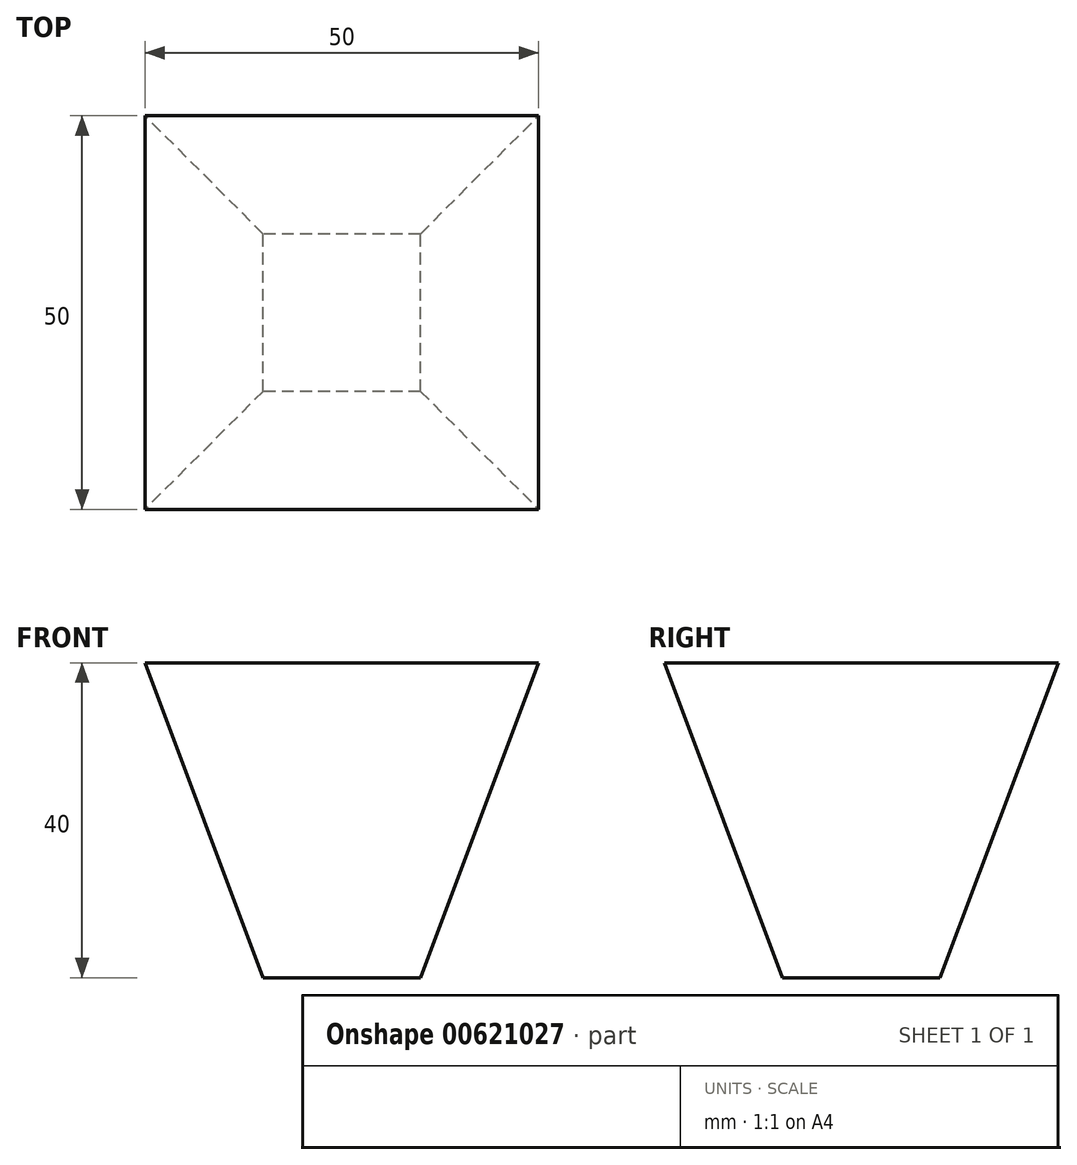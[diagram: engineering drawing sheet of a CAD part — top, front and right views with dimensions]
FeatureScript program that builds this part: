
annotation { "Feature Type Name" : "Feature", "Feature Type Description" : "" }
export const myFeature = defineFeature(function(context is Context, id is Id, definition is map)
    precondition{}
    {
        {
            var Q0;
            Q0=qCreatedBy(makeId("Top.planeOp"),FACE);
            var sketch = newSketch(context, id + "F0", { "sketchPlane" : qUnion([Q0])});
            skLineSegment(sketch, "E0.bottom", {"start": v(10, -10) * mm, "end": v(-10, -10) * mm});
            skLineSegment(sketch, "E0.top", {"start": v(10, 10) * mm, "end": v(-10, 10) * mm});
            skLineSegment(sketch, "E0.left", {"start": v(10, -10) * mm, "end": v(10, 10) * mm});
            skLineSegment(sketch, "E0.right", {"start": v(-10, -10) * mm, "end": v(-10, 10) * mm});
            skPoint(sketch, "E0.middle", {"position": v(0, 0) * mm});
            skSolve(sketch);
        }
        {
            var Q0;
            Q0=qCreatedBy(makeId("Top.planeOp"),FACE);
            cPlane(context, id + "F1", {"entities" : qUnion([Q0]), "cplaneType" : CPlaneType.OFFSET, "offset" : 40 * mm, "width" : 150 * mm, "height" : 150 * mm});
        }
        {
            var Q0;
            Q0=qCreatedBy(id+"F1.planeOp",FACE);
            var sketch = newSketch(context, id + "F2", { "sketchPlane" : qUnion([Q0])});
            skLineSegment(sketch, "E1.bottom", {"start": v(25, -25) * mm, "end": v(-25, -25) * mm});
            skLineSegment(sketch, "E1.top", {"start": v(25, 25) * mm, "end": v(-25, 25) * mm});
            skLineSegment(sketch, "E1.left", {"start": v(25, -25) * mm, "end": v(25, 25) * mm});
            skLineSegment(sketch, "E1.right", {"start": v(-25, -25) * mm, "end": v(-25, 25) * mm});
            skPoint(sketch, "E1.middle", {"position": v(0, 0) * mm});
            skSolve(sketch);
        }
        {
            var Q0;
            Q0=makeQuery(id+"F0.imprint","IMPRINT",FACE,{"disambiguationData":[TD([[makeQuery(id+"F0.imprint","IMPRINT",EDGE,{"derivedFrom":sQuery(id+"F0.wireOp",EDGE,"E0.bottom")}),-1.0]])]});
            var Q1;
            Q1=makeQuery(id+"F2.imprint","IMPRINT",FACE,{"disambiguationData":[TD([[makeQuery(id+"F2.imprint","IMPRINT",EDGE,{"derivedFrom":sQuery(id+"F2.wireOp",EDGE,"E1.bottom")}),-1.0]])]});
            loft(context, id + "F3", {"sheetProfilesArray" : [{ "sheetProfileEntities" : qUnion([Q0]) }, { "sheetProfileEntities" : qUnion([Q1]) }]});
        }
    });
